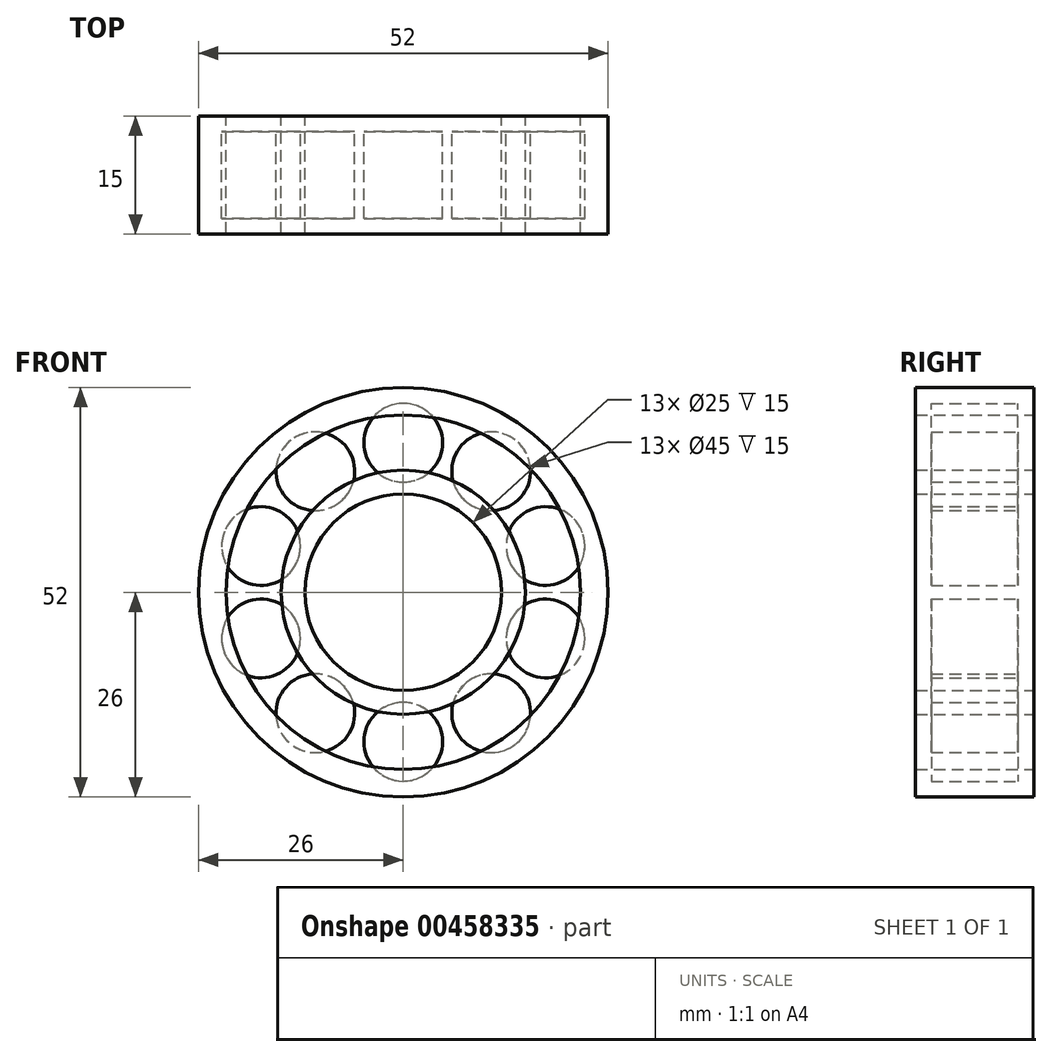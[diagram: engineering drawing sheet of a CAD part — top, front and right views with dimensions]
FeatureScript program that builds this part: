
annotation { "Feature Type Name" : "Feature", "Feature Type Description" : "" }
export const myFeature = defineFeature(function(context is Context, id is Id, definition is map)
    precondition{}
    {
        {
            var Q0;
            Q0=qCreatedBy(makeId("Front.planeOp"),FACE);
            var sketch = newSketch(context, id + "F0", { "sketchPlane" : qUnion([Q0])});
            skCircle(sketch, "E0", {"center": v(0, 0) * mm, "radius": 26 * mm});
            skCircle(sketch, "E1", {"center": v(0, 0) * mm, "radius": 22.5 * mm});
            skCircle(sketch, "E2", {"center": v(0, 0) * mm, "radius": 15.5 * mm});
            skCircle(sketch, "E3", {"center": v(0, 0) * mm, "radius": 12.5 * mm});
            skSolve(sketch);
        }
        {
            var Q0;
            Q0=makeQuery(id+"F0.imprint","IMPRINT",FACE,{"disambiguationData":[TD([[makeQuery(id+"F0.imprint","IMPRINT",EDGE,{"derivedFrom":sQuery(id+"F0.wireOp",EDGE,"E0")}),1.0]])]});
            var Q1;
            Q1=makeQuery(id+"F0.imprint","IMPRINT",FACE,{"disambiguationData":[TD([[makeQuery(id+"F0.imprint","IMPRINT",EDGE,{"derivedFrom":sQuery(id+"F0.wireOp",EDGE,"E2")}),1.0]])]});
            extrude(context, id + "F1", {"entities" : qUnion([Q0, Q1]), "depth" : 15 * mm});
        }
        {
            var Q0;
            Q0=qCreatedBy(makeId("Front.planeOp"),FACE);
            cPlane(context, id + "F2", {"entities" : qUnion([Q0]), "cplaneType" : CPlaneType.OFFSET, "offset" : 7.5 * mm, "width" : 150 * mm, "height" : 150 * mm});
        }
        {
            var Q0;
            Q0=qCreatedBy(id+"F2.planeOp",FACE);
            var sketch = newSketch(context, id + "F3", { "sketchPlane" : qUnion([Q0])});
            skCircle(sketch, "E4", {"center": v(0, 0) * mm, "radius": 19 * mm});
            skCircle(sketch, "E5", {"center": v(0, 19) * mm, "radius": 5 * mm});
            skSolve(sketch);
        }
        {
            var Q0;
            {var subQ0=sQuery(id+"F3.wireOp",EDGE,"E5");var subQ1=sQuery(id+"F3.wireOp",EDGE,"E4");var subQ2=makeQuery(id+"F3.imprint","INTERSECT",VERTEX,{"disambiguationData":[OD(0.0)],"derivedFrom":[subQ1,subQ0]});Q0=makeQuery(id+"F3.imprint","IMPRINT",FACE,{"disambiguationData":[TD([[makeQuery(id+"F3.imprint","IMPRINT",EDGE,{"disambiguationData":[TD([[subQ2,1.0]])],"derivedFrom":subQ1}),-1.0]])]});}
            var Q1;
            {var subQ0=sQuery(id+"F3.wireOp",EDGE,"E5");var subQ1=sQuery(id+"F3.wireOp",EDGE,"E4");var subQ2=makeQuery(id+"F3.imprint","INTERSECT",VERTEX,{"disambiguationData":[OD(0.0)],"derivedFrom":[subQ1,subQ0]});Q1=makeQuery(id+"F3.imprint","IMPRINT",FACE,{"disambiguationData":[TD([[makeQuery(id+"F3.imprint","IMPRINT",EDGE,{"disambiguationData":[TD([[subQ2,1.0]])],"derivedFrom":subQ1}),1.0]])]});}
            extrude(context, id + "F4", {"entities" : qUnion([Q0, Q1]), "depth" : 11 * mm, "symmetric" : true});
        }
        {
            var Q0;
            Q0=makeQuery(id+"F4.opExtrude","SWEPT_BODY",BODY,{"disambiguationData":[OSD([sQuery(id+"F3.wireOp",EDGE,"E5")])]});
            var Q1;
            Q1=makeQuery(id+"F1.opExtrude","CAP_EDGE",EDGE,{"disambiguationData":[OSD([sQuery(id+"F0.wireOp",EDGE,"E2")])],"isStart":false});
            circularPattern(context, id + "F5", {"entities" : qUnion([Q0]), "axis" : qUnion([Q1]), "angle" : 360 * degree, "instanceCount" : 10, "equalSpace" : true});
        }
    });
